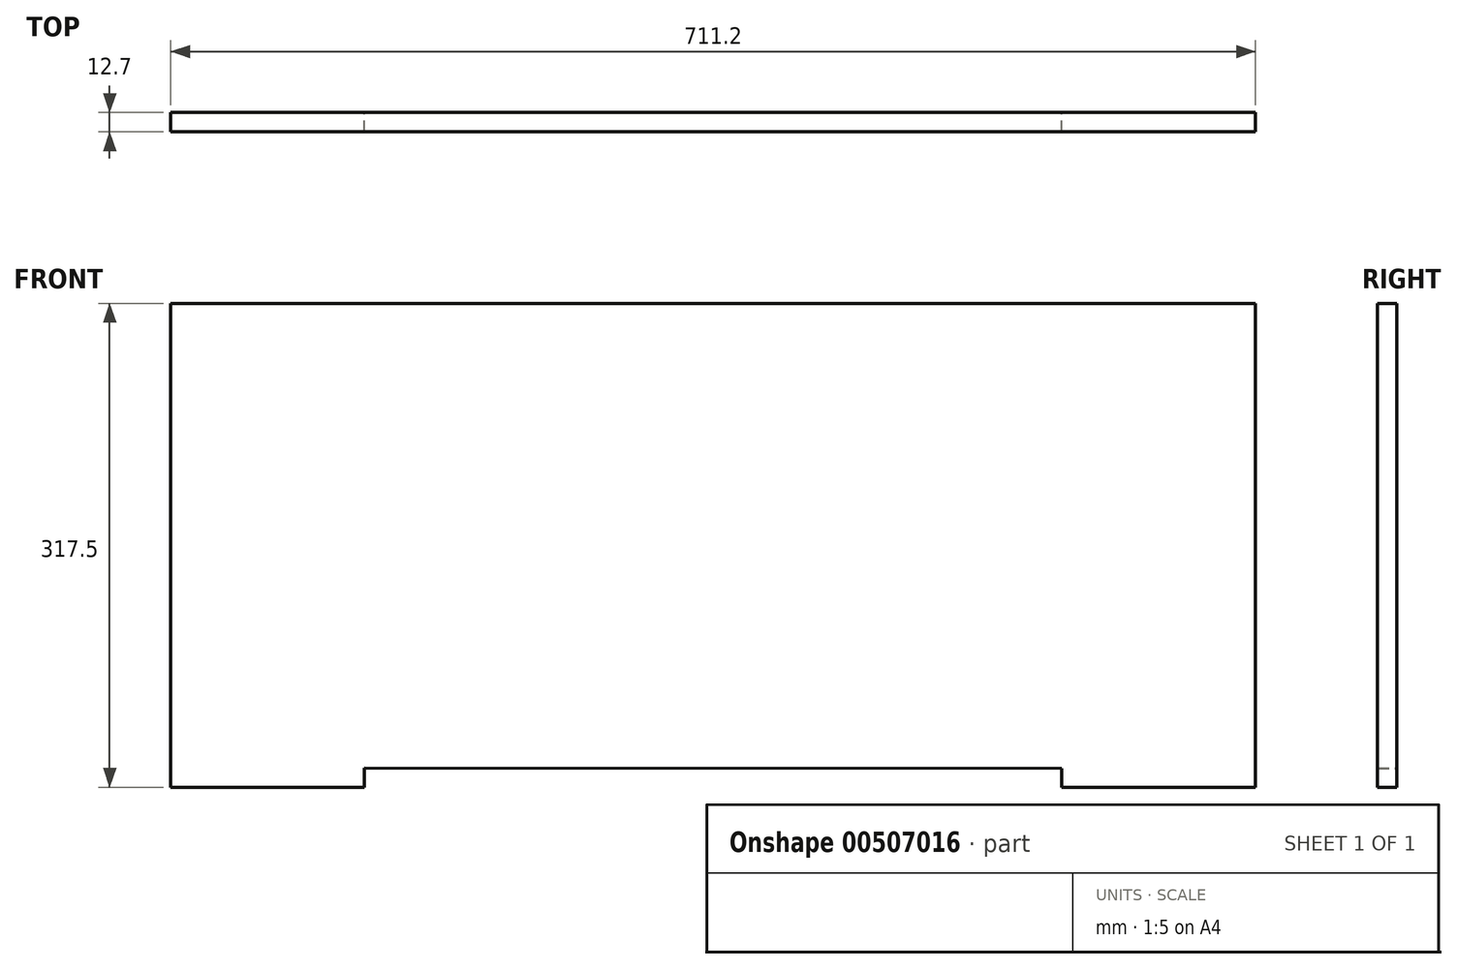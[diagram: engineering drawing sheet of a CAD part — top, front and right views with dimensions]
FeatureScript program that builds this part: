
annotation { "Feature Type Name" : "Feature", "Feature Type Description" : "" }
export const myFeature = defineFeature(function(context is Context, id is Id, definition is map)
    precondition{}
    {
        {
            var Q0;
            Q0=qCreatedBy(makeId("Front.planeOp"),FACE);
            var sketch = newSketch(context, id + "F0", { "sketchPlane" : qUnion([Q0])});
            skLineSegment(sketch, "E0", {"start": v(-444.56, 183.33) * mm, "end": v(266.64, 183.33) * mm});
            skLineSegment(sketch, "E1", {"start": v(266.64, 183.33) * mm, "end": v(266.64, -134.17) * mm});
            skLineSegment(sketch, "E2", {"start": v(-444.56, 183.33) * mm, "end": v(-444.56, -134.17) * mm});
            skLineSegment(sketch, "E3", {"start": v(-444.56, -134.17) * mm, "end": v(-317.56, -134.17) * mm});
            skLineSegment(sketch, "E4", {"start": v(-317.56, -134.17) * mm, "end": v(-317.56, -121.47) * mm});
            skLineSegment(sketch, "E5", {"start": v(139.64, -134.17) * mm, "end": v(266.64, -134.17) * mm});
            skLineSegment(sketch, "E6", {"start": v(139.64, -134.17) * mm, "end": v(139.64, -121.86) * mm});
            skLineSegment(sketch, "E7", {"start": v(139.64, -121.86) * mm, "end": v(-317.56, -121.47) * mm});
            skSolve(sketch);
        }
        {
            var Q0;
            Q0 = qSketchRegion(id + "F0", true);
            extrude(context, id + "F1", {"entities" : qUnion([Q0]), "depth" : 12.7 * mm, "offsetDistance" : 25.4 * mm});
        }
    });
